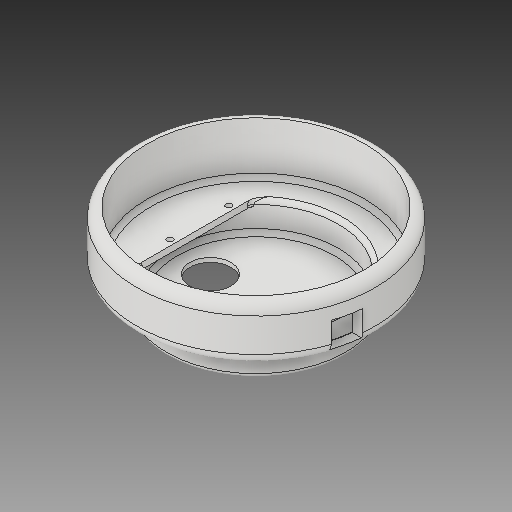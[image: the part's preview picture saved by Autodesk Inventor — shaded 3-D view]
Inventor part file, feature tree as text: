
AUTODESK INVENTOR PART (.ipt)
format: ipt  version: 2017 (Build 210142000, 142)  size: 439,296 bytes
history: native  units: mm
features: fillet x11, sketch x10, extrude x9, thicken_offset x2, hole x1, plane x1
ambient origin geometry x8: Origin, YZ Plane, XZ Plane, XY Plane, X Axis, Y Axis, Z Axis, Center Point
bodies: Solid1 (feature_tree)
feature tree (34):
  extrude  "Sensor holder"  Depth=15.0mm TaperAngle=0.0deg
  extrude  "Arduino lid"  Depth=26.0mm TaperAngle=0.0deg
  fillet  "Fillet1"  Radius=5.0mm
  fillet  "Fillet2"  Radius=5.0mm
  extrude  "Hollow arduino"  Depth=25.0mm TaperAngle=0.0deg
  fillet  "Fillet3"  Radius=79.0mm
  extrude  "Hollow sensor"  Depth=2.0mm
  fillet  "Fillet4"  Radius=2.0mm
  fillet  "Fillet5"  Radius=2.0mm
  fillet  "Fillet6"  Radius=26.665mm
  extrude  "Arduino mount points"  Depth=34.3mm
  fillet  "Fillet7"  Radius=34.3mm
  fillet  "Fillet8"  Radius=5.0mm
  fillet  "Fillet9"  Radius=5.0mm
  hole  "Arduino screw points (M3)"  [1 undecoded]
  fillet  "Fillet10"  Radius=3.0mm
  extrude  "DHT11 Sensor"  Depth=5.35mm
  plane  "Work Plane1"
  extrude  "Arduino USB"  Depth=2.0mm
  fillet  "Fillet13"  Radius=2.0mm
  extrude  "Extrusion8"  Depth=10.0mm
  thicken_offset  "Thicken1"
  thicken_offset  "Thicken2"
  extrude  "Extrusion9"  Depth=10.0mm
  sketch  "Sketch1"  dims[d0=86.0mm d1=15.0mm d2=0.0mm]
  sketch  "Sketch2"  dims[d3=114.5mm d4=26.0mm d5=0.0mm d6=5.0mm d7=5.0mm]
  sketch  "Sketch3"  dims[d8=2.0mm d9=25.0mm d10=0.0mm d11=79.0mm]
  sketch  "Sketch4"  dims[d12=14.0mm d13=0.0mm d14=2.0mm d15=2.0mm d16=2.0mm d17=26.665mm]
  sketch  "Sketch5"  dims[d18=26.665mm d19=34.3mm d20=34.3mm d21=5.0mm d22=5.0mm]
  sketch  "Sketch7"  dims[d27=18.0mm d28=5.35mm]
  sketch  "Sketch8"  dims[d29=2.0mm d30=2.0mm d31=2.0mm]
  sketch  "Sketch9"  dims[d33=2.25mm]
  sketch  "Sketch11"  dims[d34=26.665mm d35=26.665mm d36=34.3mm d37=34.3mm d44=2.25mm d45=2.9mm d46=6.0mm d47=4.0mm d48=2.0mm d49=90.0deg d50=5.0mm d51=0.0mm d52=14.9mm d54=2.3mm d55=7.0mm d56=17.4mm d57=3.1mm d58=3.1mm d59=2.0mm d61=104.5mm d62=15.1mm d63=20.0mm d64=10.0mm d65=17.0mm d66=2.0mm d67=0.0mm d71=12.5mm d72=12.5mm d73=10.0mm d74=0.0mm d77=3.0mm d78=5.7mm d79=10.0mm d88=2.115mm d89=2.115mm d91=10.0mm d92=0.0mm d93=0.2mm d94=1.0mm d98=0.2mm d99=0.2mm d101=16.8mm d102=19.72mm d103=21.86mm d104=10.0mm d105=0.0mm d80=1.0mm d81=1.0mm]
  sketch  "Sketch6"  dims[d23=4.0mm d24=4.0mm d25=3.0mm d26=0.0mm]
note: 1 required parameter value undecoded (feature->parameter linkage not recoverable at this tier; creation-order binding heuristic only, values carry confidence <= 0.55)
